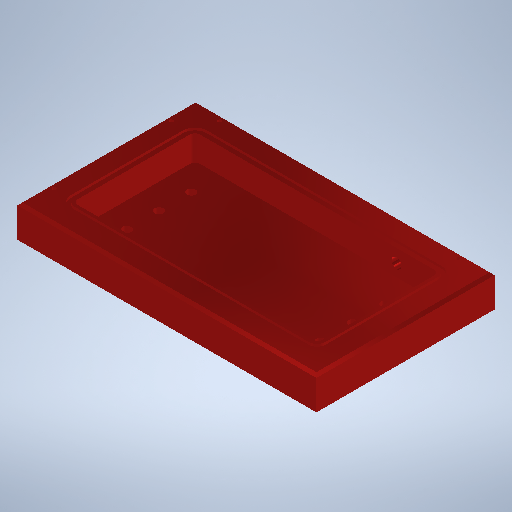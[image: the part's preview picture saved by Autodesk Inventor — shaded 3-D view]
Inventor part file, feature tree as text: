
AUTODESK INVENTOR PART (.ipt)
format: ipt  version: 2025 (Build 290162000, 162)  size: 343,040 bytes
history: native  units: mm
features: sketch x4, extrude x3, hole x3, fillet x1, chamfer x1
ambient origin geometry x8: Origin, YZ Plane, XZ Plane, XY Plane, X Axis, Y Axis, Z Axis, Center Point
bodies: Volumenkörper1 (feature_tree)
feature tree (12):
  extrude  "Extrusion1"  Depth=140.0mm
  extrude  "Extrusion2"  Depth=192.0mm
  fillet  "Rundung1"  Radius=96.0mm
  chamfer  "Fase1"  Distance=20.0mm
  sketch  "Skizze4"  dims[d10=4.0mm d11=2.0mm d12=2.0mm d13=45.0deg]
  hole  "Bohrung7"  [1 undecoded]
  hole  "Hole9"  [1 undecoded]
  extrude  "Extrusion5"  Depth=4.0mm
  hole  "Hole11"  [1 undecoded]
  sketch  "Skizze1"  dims[d0=235.0mm d2=140.0mm]
  sketch  "Skizze2"  dims[d3=25.4mm d4=0.0mm d5=192.0mm d7=96.0mm d8=20.0mm d9=0.0mm]
  sketch  "Sketch15"  dims[d153=24.0mm d154=24.0mm d155=5.0mm d158=5.0mm d159=5.0mm d160=24.0mm d161=24.0mm d162=5.0mm d169=3.0mm d170=6.0mm d171=8.0mm d172=4.6mm d173=14.3117mm d174=20.0mm d175=20.594885mm d193=76.2mm d194=76.2mm d195=6.756mm d196=6.924mm d197=12.878mm d198=2.0mm d199=14.3117mm d200=8.0mm d201=20.594885mm d202=25.4mm d203=25.4mm d204=25.4mm d205=25.4mm d220=2.5mm d221=2.5mm d222=2.5mm d225=3.0mm d226=3.0mm d227=1.905mm d228=0.0mm d229=55.0mm d230=15.0mm d231=7.9502mm d232=6.92404mm d233=0.624793mm d234=8.304022mm d235=4.0mm d236=2.0mm d237=90.0deg d238=8.0mm d239=20.594885mm]
note: 3 required parameter values undecoded (feature->parameter linkage not recoverable at this tier; creation-order binding heuristic only, values carry confidence <= 0.55)
